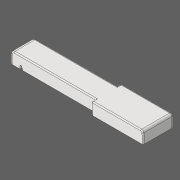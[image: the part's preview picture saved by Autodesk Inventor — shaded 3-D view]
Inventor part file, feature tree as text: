
AUTODESK INVENTOR PART (.ipt)
format: ipt  version: 2020 (Build 240168000, 168)  size: 280,064 bytes
history: native  units: in
note: dims shown in document units (in); Inventor stores cm internally (conversion verified against a paired STEP export)
features: extrude x4, other x3, fillet x2
ambient origin geometry x8: Origin, YZ Plane, XZ Plane, XY Plane, X Axis, Y Axis, Z Axis, Center Point
bodies: Solid1 (feature_tree)
feature tree (9):
  other  "Slot Start Plane"
  other  "Key Profile"
  extrude  "Upper"  TaperAngle=0.0deg  [1 undecoded]
  extrude  "Lower"  TaperAngle=0.0deg  [1 undecoded]
  extrude  "Protrusion Cutout"  Depth=0.0591in
  fillet  "Front Fillet"  Radius=0.1374in
  extrude  "Slot"  [1 undecoded]
  fillet  "Edge Softening"  Radius=0.0787in
  other  "Slot Sketch"
note: 3 required parameter values undecoded (feature->parameter linkage not recoverable at this tier; creation-order binding heuristic only, values carry confidence <= 0.55)
